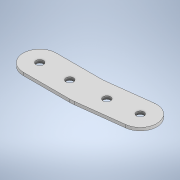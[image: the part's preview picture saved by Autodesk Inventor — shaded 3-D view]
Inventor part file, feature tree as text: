
AUTODESK INVENTOR PART (.ipt)
format: ipt  version: 2021 (Build 250183000, 183)  size: 134,656 bytes
history: native  units: mm
features: extrude x1, sketch x1
ambient origin geometry x8: Origin, YZ Plane, XZ Plane, XY Plane, X Axis, Y Axis, Z Axis, Center Point
bodies: Solid1 (feature_tree)
feature tree (2):
  extrude  "Extrusion1"  Depth=11.0mm
  sketch  "Sketch1"  dims[d0=42.0mm d3=16.929694mm d4=42.0mm d5=11.0mm d6=20.0mm d7=22.0mm d8=11.0mm d9=11.0mm d10=5.0mm d11=5.0mm d12=11.0mm d13=11.0mm d14=90.0deg d15=20.0mm d16=5.0mm d17=5.0mm d18=2.0mm d19=0.0mm d20=11.0mm d21=11.0mm]
